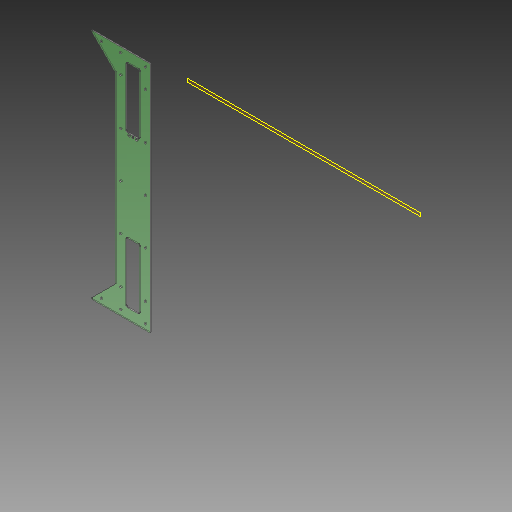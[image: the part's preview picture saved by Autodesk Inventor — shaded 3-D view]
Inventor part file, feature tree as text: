
AUTODESK INVENTOR PART (.ipt)
format: ipt  version: 2018 (Build 220112000, 112)  size: 1,100,288 bytes
history: native  units: mm
features: sketch x3, other x3, extrude x2, plane x1, hole x1, projected_geometry x1
ambient origin geometry x8: Origin, YZ Plane, XZ Plane, XY Plane, X Axis, Y Axis, Z Axis, Center Point
bodies: Solid1 (feature_tree)
feature tree (11):
  plane  "Work Plane1"
  extrude  "Extrusion1"  Depth=3.0mm TaperAngle=0.0deg
  extrude  "Extrusion2"  [1 undecoded]
  hole  "Hole1"  [1 undecoded]
  sketch  "Sketch1"  dims[d0=3.0mm d1=0.0mm d2=3.0mm d3=0.0mm]
  sketch  "Sketch2"  dims[d4=5.2mm d5=6.0mm d6=4.0mm d7=2.0mm d8=90.0deg d9=8.0mm d10=20.594885mm]
  sketch  "Sketch3"
  projected_geometry  "Projected Loop2"
  parser-record x1  (decoder bookkeeping rows leaked as tree rows — omitted from the tree; the rows remain in map.json)
  other  "Main assembly Test.iam"
  other  "3030 600mm_CPY:2"
note: 2 required parameter values undecoded (feature->parameter linkage not recoverable at this tier; creation-order binding heuristic only, values carry confidence <= 0.55)
note: 1 file-system path scrubbed to <path> (originals preserved in map.json)
